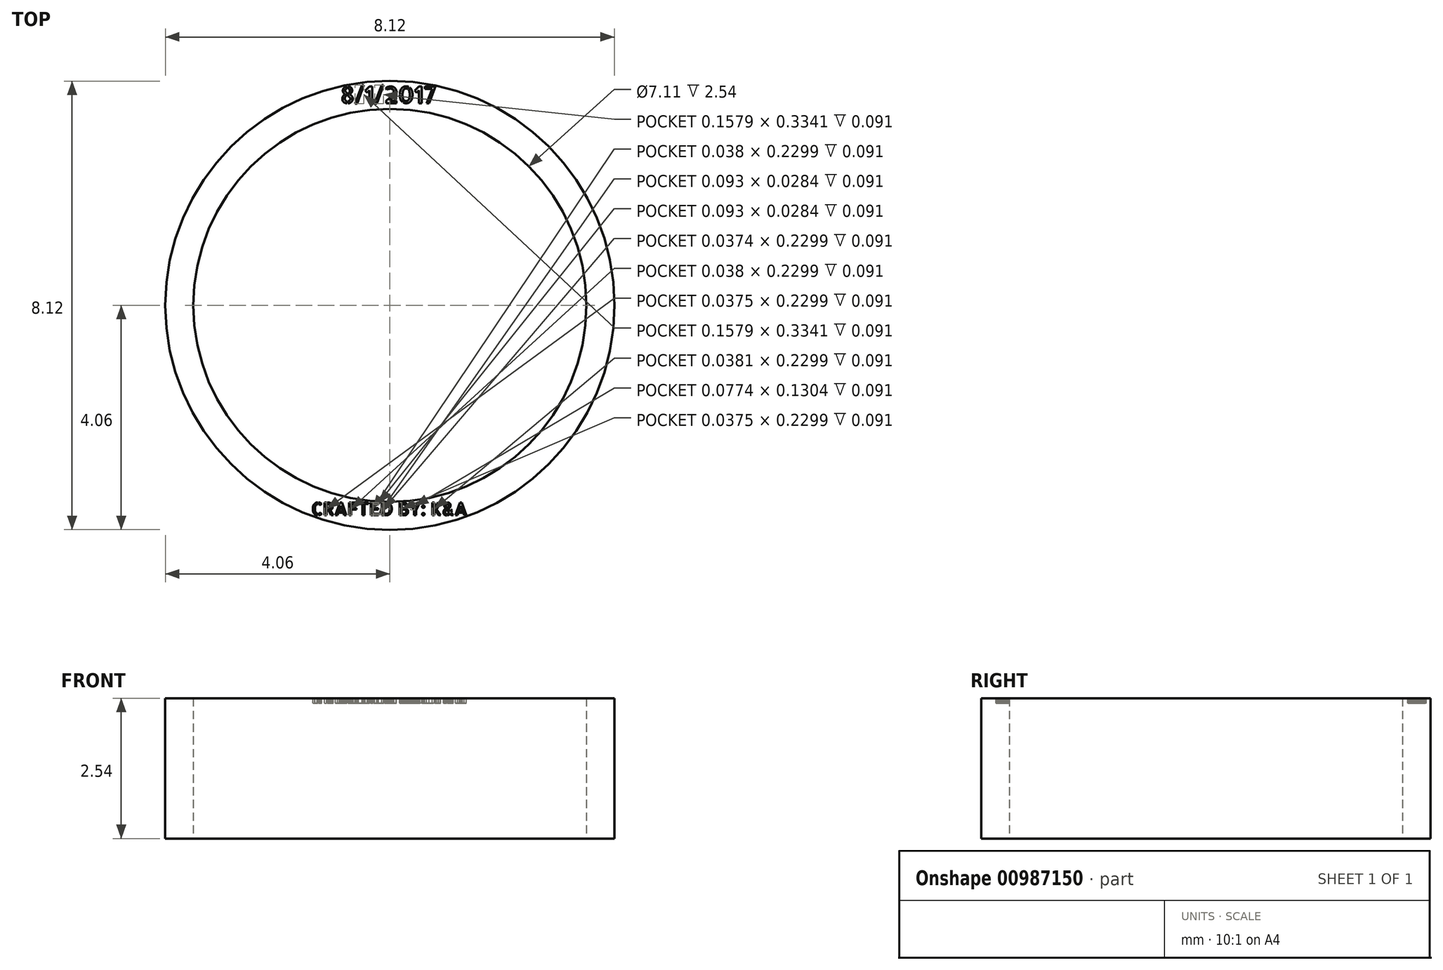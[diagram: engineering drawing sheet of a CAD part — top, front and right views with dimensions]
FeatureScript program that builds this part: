
annotation { "Feature Type Name" : "Feature", "Feature Type Description" : "" }
export const myFeature = defineFeature(function(context is Context, id is Id, definition is map)
    precondition{}
    {
        {
            var Q0;
            Q0=qCreatedBy(makeId("Top.planeOp"),FACE);
            var sketch = newSketch(context, id + "F0", { "sketchPlane" : qUnion([Q0])});
            skCircle(sketch, "E0", {"center": v(0, 0) * mm, "radius": 3.56 * mm});
            skCircle(sketch, "E1", {"center": v(0, 0) * mm, "radius": 4.06 * mm});
            skSolve(sketch);
        }
        {
            var Q0;
            Q0=makeQuery(id+"F0.imprint","IMPRINT",FACE,{"disambiguationData":[TD([[makeQuery(id+"F0.imprint","IMPRINT",EDGE,{"derivedFrom":sQuery(id+"F0.wireOp",EDGE,"E0")}),-1.0]])]});
            extrude(context, id + "F1", {"entities" : qUnion([Q0]), "depth" : 2.54 * mm, "offsetDistance" : 25.4 * mm});
        }
        {
            var Q0;
            Q0=makeQuery(id+"F1.opExtrude","CAP_FACE",FACE,{"disambiguationData":[OSD([sQuery(id+"F0.wireOp",EDGE,"E0"),sQuery(id+"F0.wireOp",EDGE,"E1")])],"isStart":false});
            var sketch = newSketch(context, id + "F2", { "sketchPlane" : qUnion([Q0])});
            skText(sketch, "E2", { "text": "CRAFTED BY: K&A", "fontName": "AllertaStencil-Regular.ttf"});
            skText(sketch, "E3", { "text": "8/1/2017\n", "fontName": "AllertaStencil-Regular.ttf"});
            const initialGuessF2  = {"E2": [-0.00142, -0.0038, 1, 0, 0.00023], "E3": [-0.00089, 0.00366, 1, 0, 0.0003]};
            skSetInitialGuess(sketch, initialGuessF2);
            skSolve(sketch);
        }
        {
            var Q0;
            Q0 = qSketchRegion(id + "F2", true);
            extrude(context, id + "F3", {"entities" : qUnion([Q0]), "operationType" : NewBodyOperationType.REMOVE, "oppositeDirection" : true, "depth" : 0.1 * mm, "offsetDistance" : 25.4 * mm});
        }
    });
